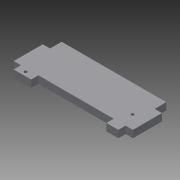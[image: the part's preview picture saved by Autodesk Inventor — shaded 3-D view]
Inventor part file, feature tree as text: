
AUTODESK INVENTOR PART (.ipt)
format: ipt  version: 2014 (Build 180170000, 170)  size: 112,640 bytes
history: native  units: mm
features: extrude x2, sketch x2
ambient origin geometry x8: Origin, YZ Plane, XZ Plane, XY Plane, X Axis, Y Axis, Z Axis, Center Point
bodies: 实体1 (feature_tree)
feature tree (4):
  extrude  "拉伸1"  Depth=72.0mm
  extrude  "拉伸2"  TaperAngle=0.0deg  [1 undecoded]
  sketch  "草图1"  dims[d0=72.0mm d1=70.2mm]
  sketch  "草图2"  dims[d2=33.0mm d3=0.0mm d4=0.0mm d5=2.0mm d6=18.9mm d7=4.6mm d8=1.5mm d9=62.2mm d10=1.5mm d11=11.4mm d12=5.0mm d13=20.0mm d14=5.0mm d15=5.0mm d16=20.0mm d17=5.0mm d18=5.0mm d19=0.0mm d20=13.1mm d21=10.0mm d22=0.0mm]
note: 1 required parameter value undecoded (feature->parameter linkage not recoverable at this tier; creation-order binding heuristic only, values carry confidence <= 0.55)
